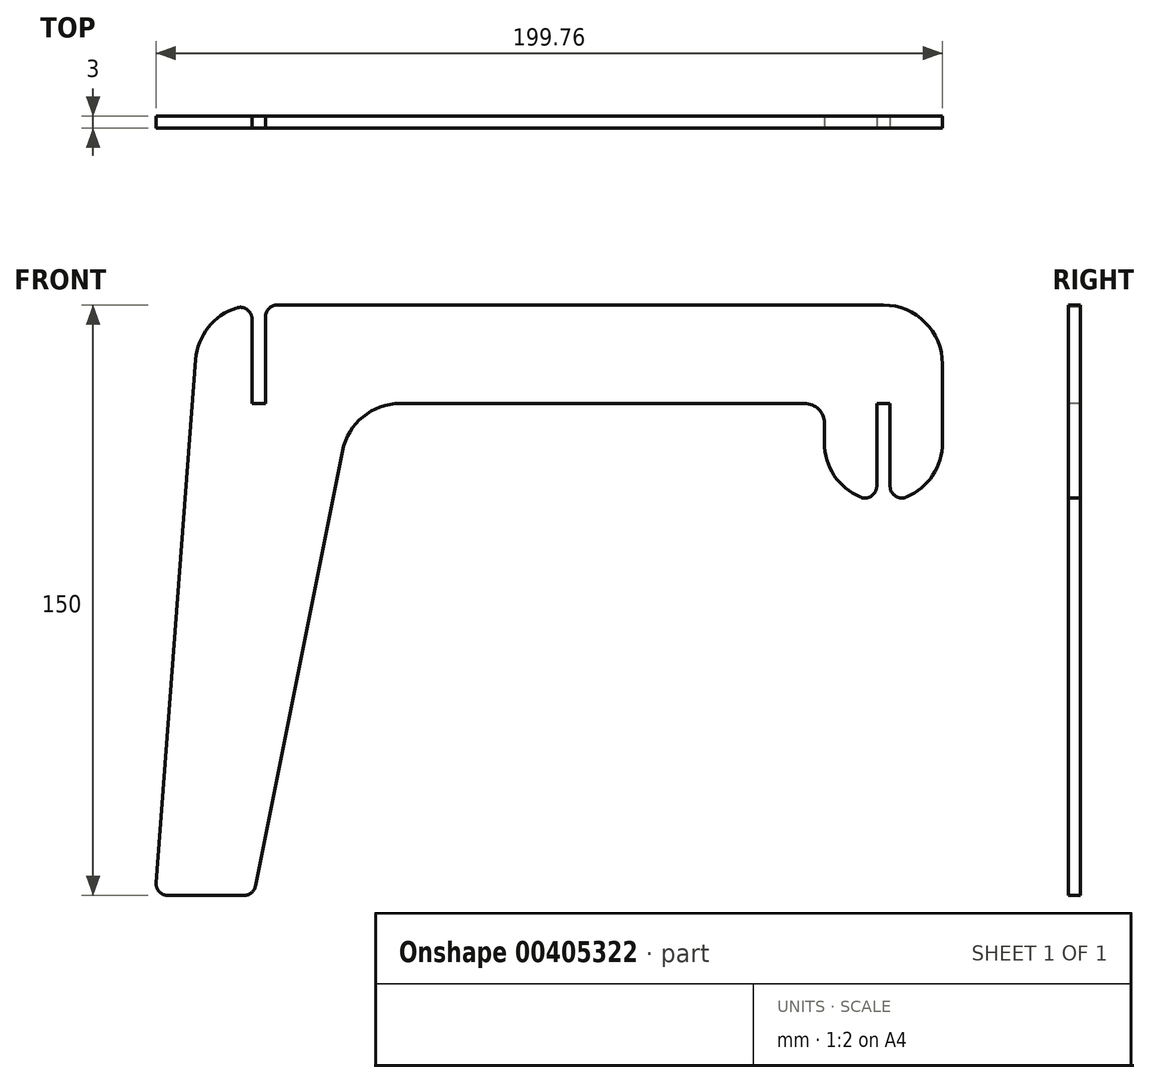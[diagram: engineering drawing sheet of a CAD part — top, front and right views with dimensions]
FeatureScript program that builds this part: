
annotation { "Feature Type Name" : "Feature", "Feature Type Description" : "" }
export const myFeature = defineFeature(function(context is Context, id is Id, definition is map)
    precondition{}
    {
        {
            var Q0;
            Q0=qCreatedBy(makeId("Front.planeOp"),FACE);
            var sketch = newSketch(context, id + "F0", { "sketchPlane" : qUnion([Q0])});
            skLineSegment(sketch, "E0.top", {"start": v(-100, -75) * mm, "end": v(-75, -75) * mm});
            skLineSegment(sketch, "E0.right", {"start": v(100, 60) * mm, "end": v(100, 50) * mm});
            skPoint(sketch, "E0.middle", {"position": v(0, 0) * mm});
            skLineSegment(sketch, "E1", {"start": v(65, 50) * mm, "end": v(-37.7, 50) * mm});
            skLineSegment(sketch, "E2", {"start": v(-52.41, 37.94) * mm, "end": v(-74.52, -72.59) * mm});
            skLineSegment(sketch, "E3", {"start": v(-77.46, -75) * mm, "end": v(-96.76, -75) * mm});
            skLineSegment(sketch, "E4", {"start": v(-99.76, -71.77) * mm, "end": v(-89.7, 61.13) * mm});
            skPoint(sketch, "E5.orphan", {"position": v(-100, 75) * mm});
            skPoint(sketch, "E6.orphan", {"position": v(100, -75) * mm});
            skPoint(sketch, "E7.visualSharp", {"position": v(-88.65, 75) * mm});
            skArc(sketch, "E7.filletArc", {"start": v(-79.32, 74.29) * mm, "mid": v(-86.52, 69.3) * mm, "end": v(-89.7, 61.13) * mm});
            skPoint(sketch, "E8.visualSharp", {"position": v(-50, 50) * mm});
            skArc(sketch, "E8.filletArc", {"start": v(-37.7, 50) * mm, "mid": v(-47.21, 46.6) * mm, "end": v(-52.41, 37.94) * mm});
            skLineSegment(sketch, "E9.left", {"start": v(100, 50) * mm, "end": v(100, 40) * mm});
            skLineSegment(sketch, "E9.right", {"start": v(70, 45) * mm, "end": v(70, 40) * mm});
            skLineSegment(sketch, "E10.top", {"start": v(83.3, 50) * mm, "end": v(86.7, 50) * mm});
            skLineSegment(sketch, "E10.left", {"start": v(83.3, 28.96) * mm, "end": v(83.3, 50) * mm});
            skLineSegment(sketch, "E10.right", {"start": v(86.7, 28.96) * mm, "end": v(86.7, 50) * mm});
            skLineSegment(sketch, "E11.top", {"start": v(-75.4, 50) * mm, "end": v(-72, 50) * mm});
            skLineSegment(sketch, "E11.left", {"start": v(-75.4, 71.43) * mm, "end": v(-75.4, 50) * mm});
            skLineSegment(sketch, "E11.right", {"start": v(-72, 72) * mm, "end": v(-72, 50) * mm});
            skLineSegment(sketch, "E12.trimOffspring", {"start": v(-69, 75) * mm, "end": v(85, 75) * mm});
            skPoint(sketch, "E13.visualSharp", {"position": v(70, 50) * mm});
            skArc(sketch, "E13.filletArc", {"start": v(70, 45) * mm, "mid": v(68.54, 48.54) * mm, "end": v(65, 50) * mm});
            skPoint(sketch, "E14.visualSharp", {"position": v(100, 75) * mm});
            skArc(sketch, "E14.filletArc", {"start": v(100, 60) * mm, "mid": v(95.6, 70.6) * mm, "end": v(85, 75) * mm});
            skPoint(sketch, "E15.visualSharp", {"position": v(100, 25) * mm});
            skArc(sketch, "E15.filletArc", {"start": v(90.88, 26.2) * mm, "mid": v(97.51, 31.73) * mm, "end": v(100, 40) * mm});
            skPoint(sketch, "E16.visualSharp", {"position": v(70, 25) * mm});
            skArc(sketch, "E16.filletArc", {"start": v(70, 40) * mm, "mid": v(72.49, 31.73) * mm, "end": v(79.13, 26.2) * mm});
            skPoint(sketch, "E17.visualSharp", {"position": v(-100, -75) * mm});
            skArc(sketch, "E17.filletArc", {"start": v(-99.76, -71.77) * mm, "mid": v(-98.96, -74.04) * mm, "end": v(-96.76, -75) * mm});
            skPoint(sketch, "E18.visualSharp", {"position": v(-75, -75) * mm});
            skArc(sketch, "E18.filletArc", {"start": v(-77.46, -75) * mm, "mid": v(-75.56, -74.32) * mm, "end": v(-74.52, -72.59) * mm});
            skArc(sketch, "E19.filletArc", {"start": v(79.13, 26.2) * mm, "mid": v(81.95, 26.46) * mm, "end": v(83.3, 28.96) * mm});
            skArc(sketch, "E20.filletArc", {"start": v(86.7, 28.96) * mm, "mid": v(88.05, 26.46) * mm, "end": v(90.88, 26.2) * mm});
            skPoint(sketch, "E21.visualSharp", {"position": v(-72, 75) * mm});
            skArc(sketch, "E21.filletArc", {"start": v(-69, 75) * mm, "mid": v(-71.13, 74.12) * mm, "end": v(-72, 72) * mm});
            skArc(sketch, "E22.filletArc", {"start": v(-75.4, 71.43) * mm, "mid": v(-76.64, 73.85) * mm, "end": v(-79.32, 74.29) * mm});
            skSolve(sketch);
        }
        {
            var Q0;
            Q0=makeQuery(id+"F0.imprint","IMPRINT",FACE,{"disambiguationData":[TD([[makeQuery(id+"F0.imprint","IMPRINT",EDGE,{"derivedFrom":sQuery(id+"F0.wireOp",EDGE,"E0.right")}),-1.0]])]});
            extrude(context, id + "F1", {"entities" : qUnion([Q0]), "oppositeDirection" : true, "depth" : 3 * mm});
        }
    });
